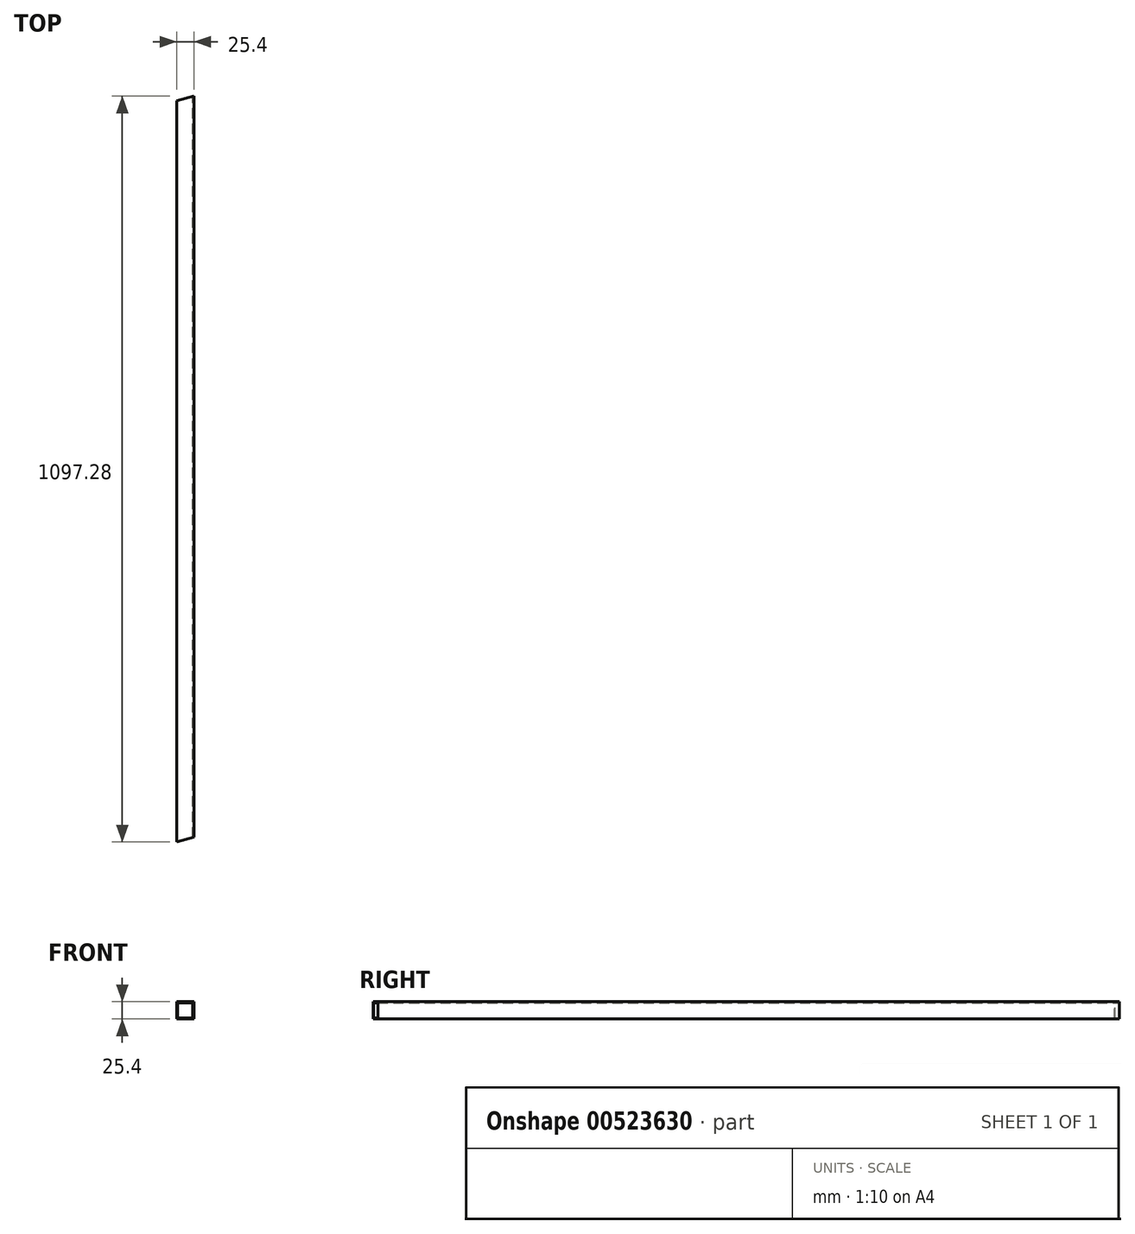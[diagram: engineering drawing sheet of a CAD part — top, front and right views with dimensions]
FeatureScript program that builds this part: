
annotation { "Feature Type Name" : "Feature", "Feature Type Description" : "" }
export const myFeature = defineFeature(function(context is Context, id is Id, definition is map)
    precondition{}
    {
        {
            var Q0;
            Q0=qCreatedBy(makeId("Front.planeOp"),FACE);
            var sketch = newSketch(context, id + "F0", { "sketchPlane" : qUnion([Q0])});
            skLineSegment(sketch, "E0.bottom", {"start": v(-12.7, -12.7) * mm, "end": v(12.7, -12.7) * mm});
            skLineSegment(sketch, "E0.top", {"start": v(-12.7, 12.7) * mm, "end": v(12.7, 12.7) * mm});
            skLineSegment(sketch, "E0.left", {"start": v(-12.7, -12.7) * mm, "end": v(-12.7, 12.7) * mm});
            skLineSegment(sketch, "E0.right", {"start": v(12.7, -12.7) * mm, "end": v(12.7, 12.7) * mm});
            skLineSegment(sketch, "E1.bottom", {"start": v(-11.11, -11.11) * mm, "end": v(11.11, -11.11) * mm});
            skLineSegment(sketch, "E1.top", {"start": v(-11.11, 11.11) * mm, "end": v(11.11, 11.11) * mm});
            skLineSegment(sketch, "E1.left", {"start": v(-11.11, -11.11) * mm, "end": v(-11.11, 11.11) * mm});
            skLineSegment(sketch, "E1.right", {"start": v(11.11, -11.11) * mm, "end": v(11.11, 11.11) * mm});
            skLineSegment(sketch, "E2", {"start": v(-11.11, 0) * mm, "end": v(11.11, 0) * mm, "construction": true});
            skLineSegment(sketch, "E3", {"start": v(0, 12.7) * mm, "end": v(0, -12.7) * mm, "construction": true});
            skSolve(sketch);
        }
        {
            var Q0;
            Q0=qSketchRegion(id+"F0",true);
            extrude(context, id + "F1", {"entities" : qUnion([Q0]), "endBound" : BoundingType.SYMMETRIC, "depth" : 1097.28 * mm, "offsetDistance" : 25.4 * mm});
        }
        {
            var Q0;
            Q0=makeQuery(id+"F1.opExtrude","SWEPT_FACE",FACE,{"disambiguationData":[OSD([sQuery(id+"F0.wireOp",EDGE,"E0.top")])]});
            var sketch = newSketch(context, id + "F2", { "sketchPlane" : qUnion([Q0])});
            skLineSegment(sketch, "E4", {"start": v(-12.7, 548.64) * mm, "end": v(-12.7, 541.7) * mm});
            skLineSegment(sketch, "E5", {"start": v(-12.7, 541.7) * mm, "end": v(12.7, 548.64) * mm});
            skLineSegment(sketch, "E6", {"start": v(12.7, 548.64) * mm, "end": v(-12.7, 548.64) * mm});
            skSolve(sketch);
        }
        {
            var Q0;
            Q0=qSketchRegion(id+"F2",true);
            extrude(context, id + "F3", {"entities" : qUnion([Q0]), "operationType" : NewBodyOperationType.REMOVE, "endBound" : BoundingType.THROUGH_ALL, "oppositeDirection" : true, "depth" : 25.4 * mm, "offsetDistance" : 25.4 * mm});
        }
        {
            var Q0;
            Q0=makeQuery(id+"F1.opExtrude","SWEPT_FACE",FACE,{"disambiguationData":[OSD([sQuery(id+"F0.wireOp",EDGE,"E0.top")])]});
            var sketch = newSketch(context, id + "F4", { "sketchPlane" : qUnion([Q0])});
            skLineSegment(sketch, "E7", {"start": v(-12.7, -548.64) * mm, "end": v(12.7, -541.7) * mm});
            skLineSegment(sketch, "E8", {"start": v(12.7, -541.7) * mm, "end": v(12.7, -548.64) * mm});
            skLineSegment(sketch, "E9", {"start": v(12.7, -548.64) * mm, "end": v(-12.7, -548.64) * mm});
            skSolve(sketch);
        }
        {
            var Q0;
            Q0=qSketchRegion(id+"F4",true);
            extrude(context, id + "F5", {"entities" : qUnion([Q0]), "operationType" : NewBodyOperationType.REMOVE, "endBound" : BoundingType.THROUGH_ALL, "oppositeDirection" : true, "depth" : 25.4 * mm, "offsetDistance" : 25.4 * mm});
        }
    });
